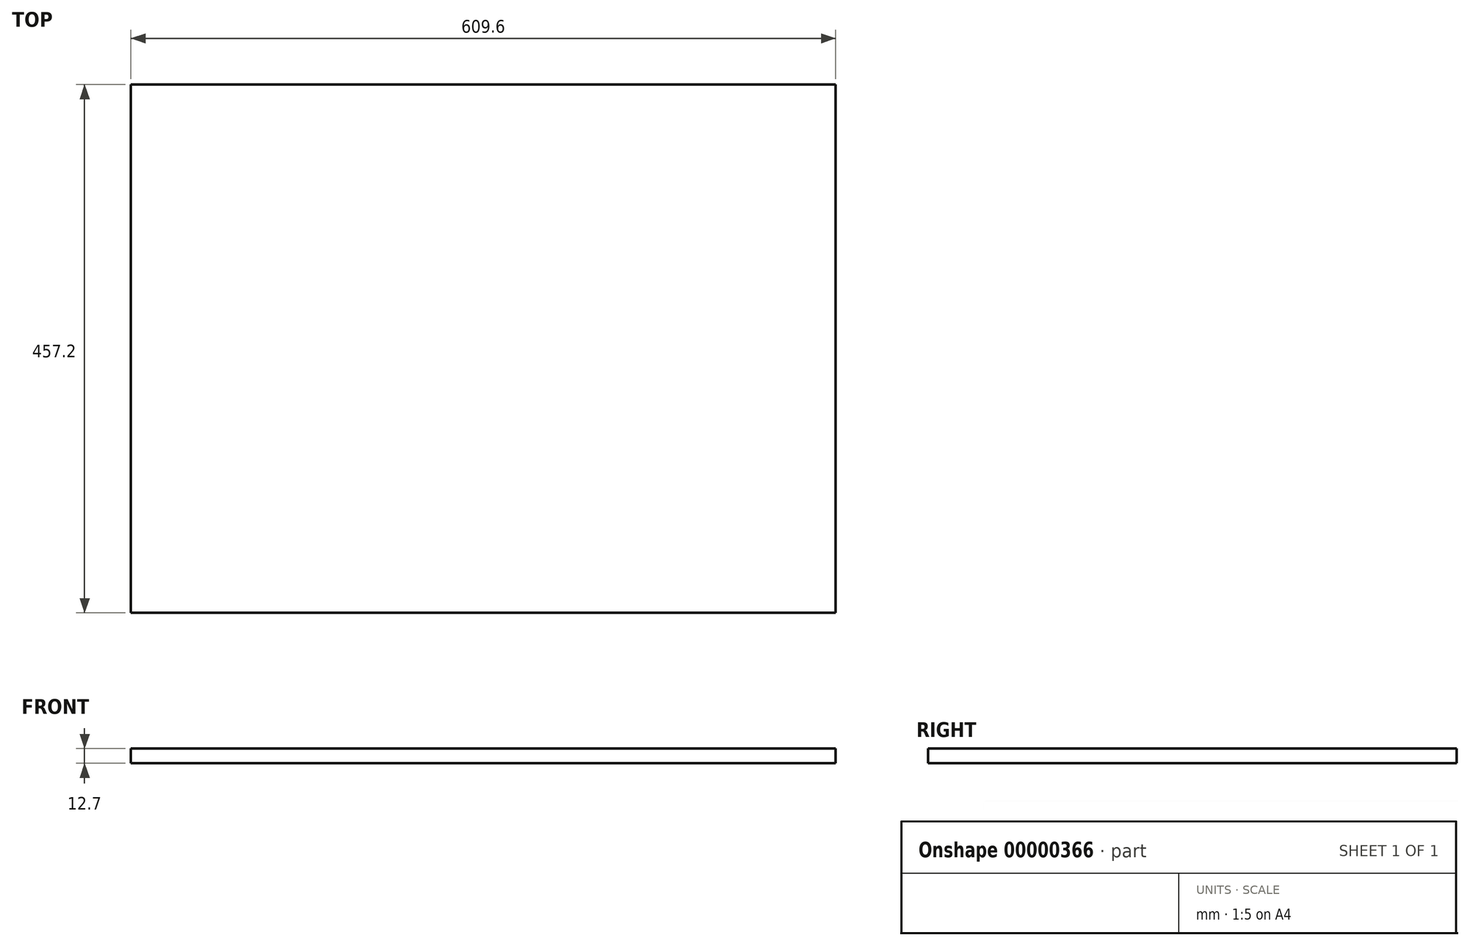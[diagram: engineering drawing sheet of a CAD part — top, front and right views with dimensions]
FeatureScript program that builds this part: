
annotation { "Feature Type Name" : "Feature", "Feature Type Description" : "" }
export const myFeature = defineFeature(function(context is Context, id is Id, definition is map)
    precondition{}
    {
        {
            var Q0;
            Q0=qCreatedBy(makeId("Top.planeOp"),FACE);
            var sketch = newSketch(context, id + "F0", { "sketchPlane" : qUnion([Q0])});
            skLineSegment(sketch, "E0.bottom", {"start": v(304.8, -228.6) * mm, "end": v(-304.8, -228.6) * mm});
            skLineSegment(sketch, "E0.top", {"start": v(304.8, 228.6) * mm, "end": v(-304.8, 228.6) * mm});
            skLineSegment(sketch, "E0.left", {"start": v(304.8, -228.6) * mm, "end": v(304.8, 228.6) * mm});
            skLineSegment(sketch, "E0.right", {"start": v(-304.8, -228.6) * mm, "end": v(-304.8, 228.6) * mm});
            skPoint(sketch, "E0.middle", {"position": v(0, 0) * mm});
            skSolve(sketch);
        }
        {
            var Q0;
            Q0 = qSketchRegion(id + "F0", true);
            extrude(context, id + "F1", {"entities" : qUnion([Q0]), "depth" : 12.7 * mm});
        }
    });
